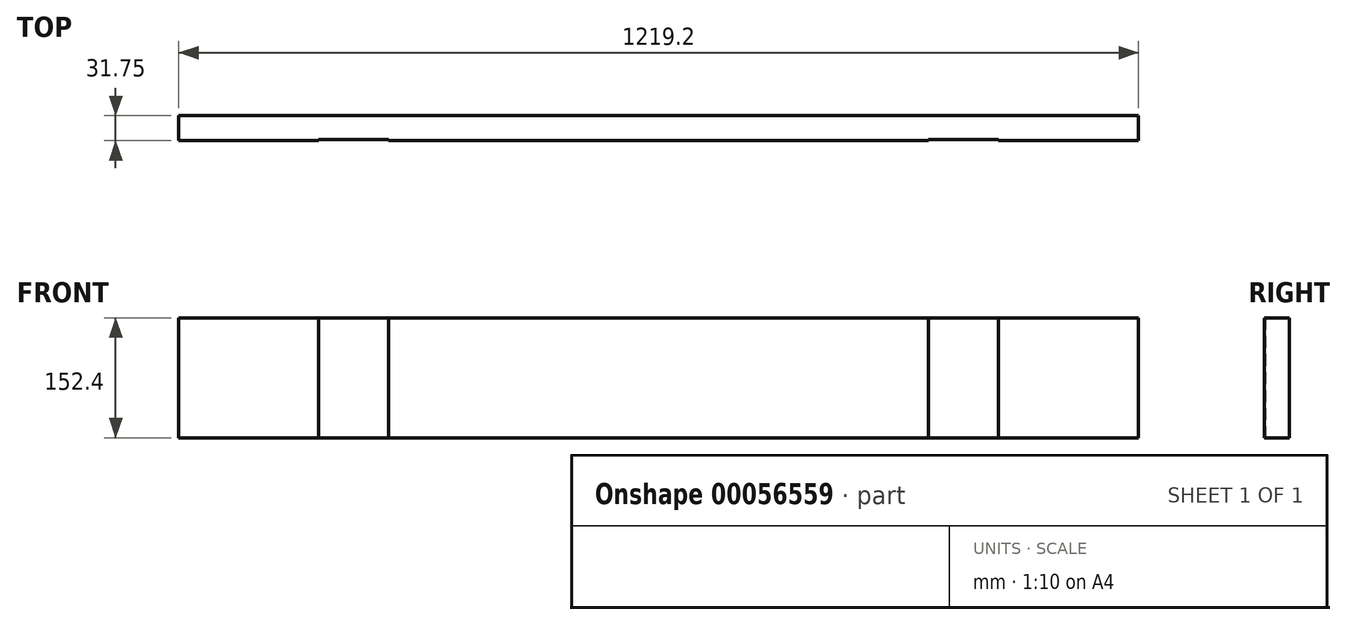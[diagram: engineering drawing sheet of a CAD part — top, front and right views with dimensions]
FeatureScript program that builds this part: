
annotation { "Feature Type Name" : "Feature", "Feature Type Description" : "" }
export const myFeature = defineFeature(function(context is Context, id is Id, definition is map)
    precondition{}
    {
        {
            var Q0;
            Q0=qCreatedBy(makeId("Front.planeOp"),FACE);
            var sketch = newSketch(context, id + "F0", { "sketchPlane" : qUnion([Q0])});
            skLineSegment(sketch, "E0.bottom", {"start": v(0, 0) * mm, "end": v(-1219.2, 0) * mm});
            skLineSegment(sketch, "E0.top", {"start": v(0, 152.4) * mm, "end": v(-1219.2, 152.4) * mm});
            skLineSegment(sketch, "E0.left", {"start": v(0, 0) * mm, "end": v(0, 152.4) * mm});
            skLineSegment(sketch, "E0.right", {"start": v(-1219.2, 0) * mm, "end": v(-1219.2, 152.4) * mm});
            skSolve(sketch);
        }
        {
            var Q0;
            Q0=makeQuery(id+"F0.imprint","IMPRINT",FACE,{"disambiguationData":[TD([[makeQuery(id+"F0.imprint","IMPRINT",EDGE,{"derivedFrom":sQuery(id+"F0.wireOp",EDGE,"E0.bottom")}),-1.0]])]});
            extrude(context, id + "F1", {"entities" : qUnion([Q0]), "depth" : 31.75 * mm});
        }
        {
            var Q0;
            Q0=makeQuery(id+"F1.opExtrude","CAP_FACE",FACE,{"disambiguationData":[OSD([sQuery(id+"F0.wireOp",EDGE,"E0.bottom"),sQuery(id+"F0.wireOp",EDGE,"E0.top"),sQuery(id+"F0.wireOp",EDGE,"E0.left"),sQuery(id+"F0.wireOp",EDGE,"E0.right")])],"isStart":false});
            var sketch = newSketch(context, id + "F2", { "sketchPlane" : qUnion([Q0])});
            skLineSegment(sketch, "E1.bottom", {"start": v(-1219.2, 152.4) * mm, "end": v(-1041.4, 152.4) * mm});
            skLineSegment(sketch, "E1.top", {"start": v(-1219.2, 0) * mm, "end": v(-1041.4, 0) * mm});
            skLineSegment(sketch, "E1.left", {"start": v(-1219.2, 152.4) * mm, "end": v(-1219.2, 0) * mm});
            skLineSegment(sketch, "E1.right", {"start": v(-1041.4, 152.4) * mm, "end": v(-1041.4, 0) * mm});
            skLineSegment(sketch, "E2.bottom", {"start": v(0, 152.4) * mm, "end": v(-177.8, 152.4) * mm});
            skLineSegment(sketch, "E2.top", {"start": v(0, 0) * mm, "end": v(-177.8, 0) * mm});
            skLineSegment(sketch, "E2.left", {"start": v(0, 152.4) * mm, "end": v(0, 0) * mm});
            skLineSegment(sketch, "E2.right", {"start": v(-177.8, 152.4) * mm, "end": v(-177.8, 0) * mm});
            skLineSegment(sketch, "E3.bottom", {"start": v(-1041.4, 152.4) * mm, "end": v(-952.5, 152.4) * mm});
            skLineSegment(sketch, "E3.top", {"start": v(-1041.4, 0) * mm, "end": v(-952.5, 0) * mm});
            skLineSegment(sketch, "E3.right", {"start": v(-952.5, 152.4) * mm, "end": v(-952.5, 0) * mm});
            skLineSegment(sketch, "E4.bottom", {"start": v(-177.8, 152.4) * mm, "end": v(-266.7, 152.4) * mm});
            skLineSegment(sketch, "E4.top", {"start": v(-177.8, 0) * mm, "end": v(-266.7, 0) * mm});
            skLineSegment(sketch, "E4.right", {"start": v(-266.7, 152.4) * mm, "end": v(-266.7, 0) * mm});
            skSolve(sketch);
        }
        {
            var Q0;
            Q0=makeQuery(id+"F2.imprint","IMPRINT",FACE,{"disambiguationData":[TD([[makeQuery(id+"F2.imprint","IMPRINT",EDGE,{"derivedFrom":sQuery(id+"F2.wireOp",EDGE,"E3.bottom")}),1.0]])]});
            extrude(context, id + "F3", {"entities" : qUnion([Q0]), "operationType" : NewBodyOperationType.REMOVE, "oppositeDirection" : true, "depth" : 1.27 * mm});
        }
        {
            var Q0;
            Q0=makeQuery(id+"F2.imprint","IMPRINT",FACE,{"disambiguationData":[TD([[makeQuery(id+"F2.imprint","IMPRINT",EDGE,{"derivedFrom":sQuery(id+"F2.wireOp",EDGE,"E4.bottom")}),1.0]])]});
            extrude(context, id + "F4", {"entities" : qUnion([Q0]), "operationType" : NewBodyOperationType.REMOVE, "oppositeDirection" : true, "depth" : 1.27 * mm});
        }
    });
